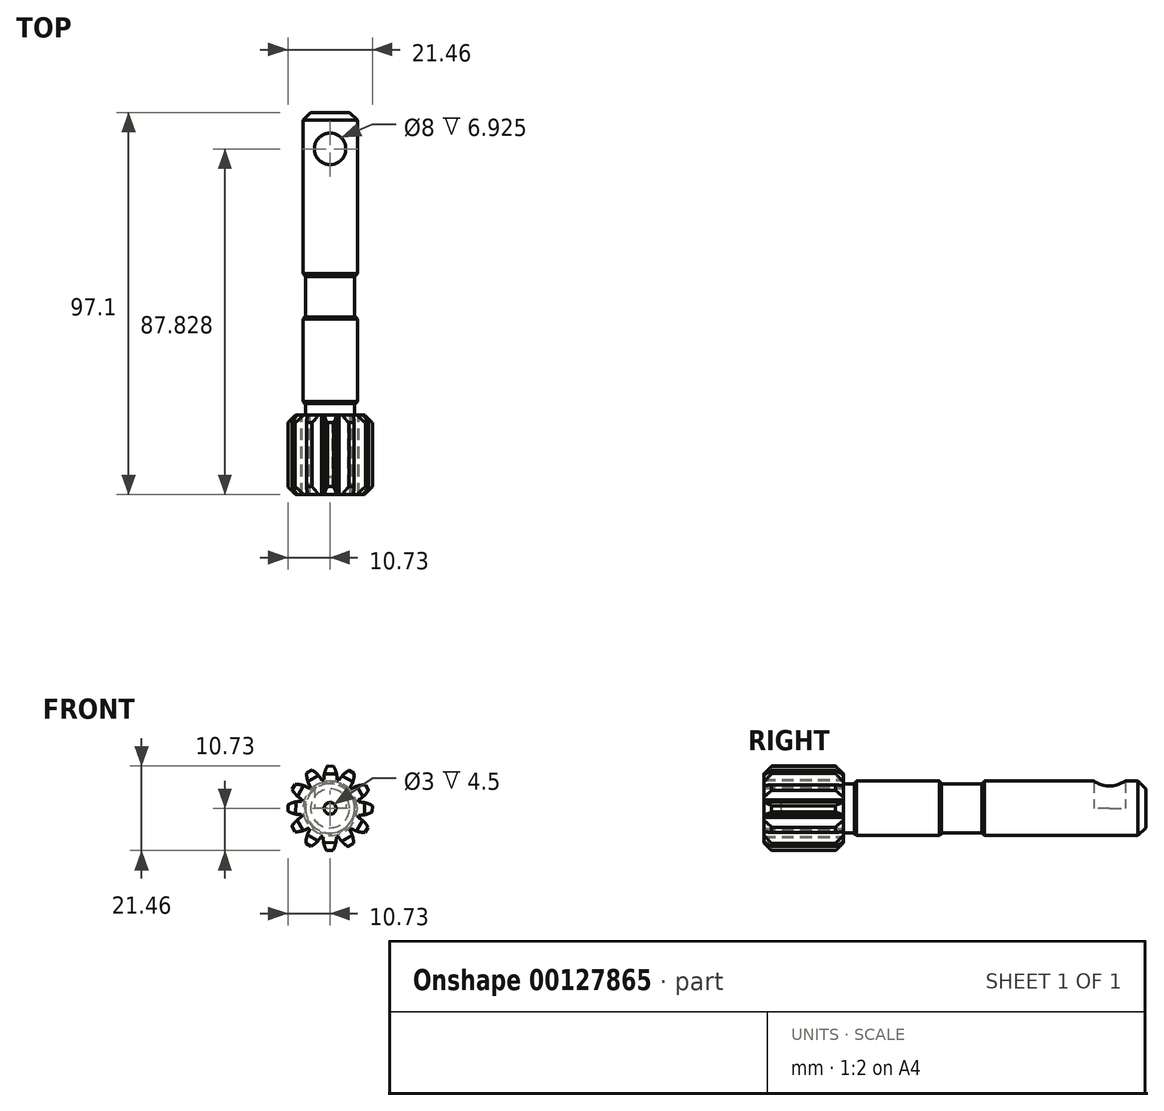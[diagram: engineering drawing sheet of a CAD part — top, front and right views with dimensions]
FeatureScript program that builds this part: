
annotation { "Feature Type Name" : "Feature", "Feature Type Description" : "" }
export const myFeature = defineFeature(function(context is Context, id is Id, definition is map)
    precondition{}
    {
        {
            var Q0;
            Q0=qCreatedBy(makeId("Front.planeOp"),FACE);
            var sketch = newSketch(context, id + "F0", { "sketchPlane" : qUnion([Q0])});
            skCircle(sketch, "E0", {"center": v(0, 0) * mm, "radius": 7.5 * mm});
            skCircle(sketch, "E1", {"center": v(0, 0) * mm, "radius": 10.75 * mm, "construction": true});
            skCircle(sketch, "E2", {"center": v(0, 0) * mm, "radius": 8.75 * mm, "construction": true});
            skArc(sketch, "E3", {"start": v(-0.67, 10.73) * mm, "mid": v(-1.38, 9.1) * mm, "end": v(-1.58, 7.33) * mm});
            skArc(sketch, "E4", {"start": v(1.73, 7.3) * mm, "mid": v(1.56, 9.07) * mm, "end": v(0.88, 10.71) * mm});
            skLineSegment(sketch, "E5", {"start": v(-0.67, 10.73) * mm, "end": v(0.88, 10.71) * mm});
            skLineSegment(sketch, "E6.1.0", {"start": v(-5.95, 8.95) * mm, "end": v(-4.6, 9.72) * mm});
            skArc(sketch, "E6.1.1", {"start": v(-2.15, 7.19) * mm, "mid": v(-3.18, 8.63) * mm, "end": v(-4.6, 9.72) * mm});
            skArc(sketch, "E6.1.2", {"start": v(-5.95, 8.95) * mm, "mid": v(-5.75, 7.19) * mm, "end": v(-5.04, 5.56) * mm});
            skLineSegment(sketch, "E6.2.0", {"start": v(-9.63, 4.78) * mm, "end": v(-8.84, 6.12) * mm});
            skArc(sketch, "E6.2.1", {"start": v(-5.45, 5.15) * mm, "mid": v(-7.07, 5.89) * mm, "end": v(-8.84, 6.12) * mm});
            skArc(sketch, "E6.2.2", {"start": v(-9.63, 4.78) * mm, "mid": v(-8.57, 3.35) * mm, "end": v(-7.14, 2.3) * mm});
            skLineSegment(sketch, "E6.3.0", {"start": v(-10.73, -0.67) * mm, "end": v(-10.71, 0.88) * mm});
            skArc(sketch, "E6.3.1", {"start": v(-7.3, 1.73) * mm, "mid": v(-9.07, 1.56) * mm, "end": v(-10.71, 0.88) * mm});
            skArc(sketch, "E6.3.2", {"start": v(-10.73, -0.67) * mm, "mid": v(-9.1, -1.38) * mm, "end": v(-7.33, -1.58) * mm});
            skLineSegment(sketch, "E6.4.0", {"start": v(-8.95, -5.95) * mm, "end": v(-9.72, -4.6) * mm});
            skArc(sketch, "E6.4.1", {"start": v(-7.19, -2.15) * mm, "mid": v(-8.63, -3.18) * mm, "end": v(-9.72, -4.6) * mm});
            skArc(sketch, "E6.4.2", {"start": v(-8.95, -5.95) * mm, "mid": v(-7.19, -5.75) * mm, "end": v(-5.56, -5.04) * mm});
            skLineSegment(sketch, "E6.5.0", {"start": v(-4.78, -9.63) * mm, "end": v(-6.12, -8.84) * mm});
            skArc(sketch, "E6.5.1", {"start": v(-5.15, -5.45) * mm, "mid": v(-5.89, -7.07) * mm, "end": v(-6.12, -8.84) * mm});
            skArc(sketch, "E6.5.2", {"start": v(-4.78, -9.63) * mm, "mid": v(-3.35, -8.57) * mm, "end": v(-2.3, -7.14) * mm});
            skLineSegment(sketch, "E6.6.0", {"start": v(0.67, -10.73) * mm, "end": v(-0.88, -10.71) * mm});
            skArc(sketch, "E6.6.1", {"start": v(-1.73, -7.3) * mm, "mid": v(-1.56, -9.07) * mm, "end": v(-0.88, -10.71) * mm});
            skArc(sketch, "E6.6.2", {"start": v(0.67, -10.73) * mm, "mid": v(1.38, -9.1) * mm, "end": v(1.58, -7.33) * mm});
            skLineSegment(sketch, "E6.7.0", {"start": v(5.95, -8.95) * mm, "end": v(4.6, -9.72) * mm});
            skArc(sketch, "E6.7.1", {"start": v(2.15, -7.19) * mm, "mid": v(3.18, -8.63) * mm, "end": v(4.6, -9.72) * mm});
            skArc(sketch, "E6.7.2", {"start": v(5.95, -8.95) * mm, "mid": v(5.75, -7.19) * mm, "end": v(5.04, -5.56) * mm});
            skLineSegment(sketch, "E6.8.0", {"start": v(9.63, -4.78) * mm, "end": v(8.84, -6.12) * mm});
            skArc(sketch, "E6.8.1", {"start": v(5.45, -5.15) * mm, "mid": v(7.07, -5.89) * mm, "end": v(8.84, -6.12) * mm});
            skArc(sketch, "E6.8.2", {"start": v(9.63, -4.78) * mm, "mid": v(8.57, -3.35) * mm, "end": v(7.14, -2.3) * mm});
            skLineSegment(sketch, "E6.9.0", {"start": v(10.73, 0.67) * mm, "end": v(10.71, -0.88) * mm});
            skArc(sketch, "E6.9.1", {"start": v(7.3, -1.73) * mm, "mid": v(9.07, -1.56) * mm, "end": v(10.71, -0.88) * mm});
            skArc(sketch, "E6.9.2", {"start": v(10.73, 0.67) * mm, "mid": v(9.1, 1.38) * mm, "end": v(7.33, 1.58) * mm});
            skLineSegment(sketch, "E6.10.0", {"start": v(8.95, 5.95) * mm, "end": v(9.72, 4.6) * mm});
            skArc(sketch, "E6.10.1", {"start": v(7.19, 2.15) * mm, "mid": v(8.63, 3.18) * mm, "end": v(9.72, 4.6) * mm});
            skArc(sketch, "E6.10.2", {"start": v(8.95, 5.95) * mm, "mid": v(7.19, 5.75) * mm, "end": v(5.56, 5.04) * mm});
            skLineSegment(sketch, "E6.11.0", {"start": v(4.78, 9.63) * mm, "end": v(6.12, 8.84) * mm});
            skArc(sketch, "E6.11.1", {"start": v(5.15, 5.45) * mm, "mid": v(5.89, 7.07) * mm, "end": v(6.12, 8.84) * mm});
            skArc(sketch, "E6.11.2", {"start": v(4.78, 9.63) * mm, "mid": v(3.35, 8.57) * mm, "end": v(2.3, 7.14) * mm});
            skSolve(sketch);
        }
        {
            var Q0;
            {var subQ0=sQuery(id+"F0.wireOp",EDGE,"E3");Q0=makeQuery(id+"F0.imprint","IMPRINT",FACE,{"disambiguationData":[TD([[makeQuery(id+"F0.imprint","IMPRINT",EDGE,{"derivedFrom":subQ0}),1.0]])]});}
            var Q1;
            {var subQ0=sQuery(id+"F0.wireOp",EDGE,"E0");var subQ15=makeQuery(id+"F0.imprint","INTERSECT",VERTEX,{"derivedFrom":[subQ0,sQuery(id+"F0.wireOp",EDGE,"E6.9.2")]});Q1=makeQuery(id+"F0.imprint","IMPRINT",FACE,{"disambiguationData":[TD([[makeQuery(id+"F0.imprint","IMPRINT",EDGE,{"disambiguationData":[TD([[subQ15,-1.0]])],"derivedFrom":subQ0}),1.0]])]});}
            var Q2;
            Q2=makeQuery(id+"F0.imprint","IMPRINT",FACE,{"disambiguationData":[TD([[makeQuery(id+"F0.imprint","IMPRINT",EDGE,{"derivedFrom":sQuery(id+"F0.wireOp",EDGE,"E6.4.0")}),-1.0]])]});
            var Q3;
            Q3=makeQuery(id+"F0.imprint","IMPRINT",FACE,{"disambiguationData":[TD([[makeQuery(id+"F0.imprint","IMPRINT",EDGE,{"derivedFrom":sQuery(id+"F0.wireOp",EDGE,"E6.3.0")}),-1.0]])]});
            var Q4;
            Q4=makeQuery(id+"F0.imprint","IMPRINT",FACE,{"disambiguationData":[TD([[makeQuery(id+"F0.imprint","IMPRINT",EDGE,{"derivedFrom":sQuery(id+"F0.wireOp",EDGE,"E6.2.0")}),-1.0]])]});
            var Q5;
            Q5=makeQuery(id+"F0.imprint","IMPRINT",FACE,{"disambiguationData":[TD([[makeQuery(id+"F0.imprint","IMPRINT",EDGE,{"derivedFrom":sQuery(id+"F0.wireOp",EDGE,"E6.1.0")}),-1.0]])]});
            var Q6;
            Q6=makeQuery(id+"F0.imprint","IMPRINT",FACE,{"disambiguationData":[TD([[makeQuery(id+"F0.imprint","IMPRINT",EDGE,{"derivedFrom":sQuery(id+"F0.wireOp",EDGE,"E6.5.0")}),-1.0]])]});
            var Q7;
            Q7=makeQuery(id+"F0.imprint","IMPRINT",FACE,{"disambiguationData":[TD([[makeQuery(id+"F0.imprint","IMPRINT",EDGE,{"derivedFrom":sQuery(id+"F0.wireOp",EDGE,"E6.6.0")}),-1.0]])]});
            var Q8;
            Q8=makeQuery(id+"F0.imprint","IMPRINT",FACE,{"disambiguationData":[TD([[makeQuery(id+"F0.imprint","IMPRINT",EDGE,{"derivedFrom":sQuery(id+"F0.wireOp",EDGE,"E6.7.0")}),-1.0]])]});
            var Q9;
            Q9=makeQuery(id+"F0.imprint","IMPRINT",FACE,{"disambiguationData":[TD([[makeQuery(id+"F0.imprint","IMPRINT",EDGE,{"derivedFrom":sQuery(id+"F0.wireOp",EDGE,"E6.8.0")}),-1.0]])]});
            var Q10;
            Q10=makeQuery(id+"F0.imprint","IMPRINT",FACE,{"disambiguationData":[TD([[makeQuery(id+"F0.imprint","IMPRINT",EDGE,{"derivedFrom":sQuery(id+"F0.wireOp",EDGE,"E6.9.0")}),-1.0]])]});
            var Q11;
            Q11=makeQuery(id+"F0.imprint","IMPRINT",FACE,{"disambiguationData":[TD([[makeQuery(id+"F0.imprint","IMPRINT",EDGE,{"derivedFrom":sQuery(id+"F0.wireOp",EDGE,"E6.10.0")}),-1.0]])]});
            var Q12;
            Q12=makeQuery(id+"F0.imprint","IMPRINT",FACE,{"disambiguationData":[TD([[makeQuery(id+"F0.imprint","IMPRINT",EDGE,{"derivedFrom":sQuery(id+"F0.wireOp",EDGE,"E6.11.0")}),-1.0]])]});
            extrude(context, id + "F1", {"entities" : qUnion([Q0, Q1, Q2, Q3, Q4, Q5, Q6, Q7, Q8, Q9, Q10, Q11, Q12]), "depth" : 20.25 * mm});
        }
        {
            var Q0;
            Q0=makeQuery(id+"F1.opExtrude","CAP_EDGE",EDGE,{"disambiguationData":[OSD([sQuery(id+"F0.wireOp",EDGE,"E6.11.0")])],"isStart":true});
            var Q1;
            Q1=makeQuery(id+"F1.opExtrude","CAP_EDGE",EDGE,{"disambiguationData":[OSD([sQuery(id+"F0.wireOp",EDGE,"E6.11.0")])],"isStart":false});
            var Q2;
            Q2=makeQuery(id+"F1.opExtrude","CAP_EDGE",EDGE,{"disambiguationData":[OSD([sQuery(id+"F0.wireOp",EDGE,"E5")])],"isStart":false});
            var Q3;
            Q3=makeQuery(id+"F1.opExtrude","CAP_EDGE",EDGE,{"disambiguationData":[OSD([sQuery(id+"F0.wireOp",EDGE,"E5")])],"isStart":true});
            var Q4;
            Q4=makeQuery(id+"F1.opExtrude","CAP_EDGE",EDGE,{"disambiguationData":[OSD([sQuery(id+"F0.wireOp",EDGE,"E6.1.0")])],"isStart":false});
            var Q5;
            Q5=makeQuery(id+"F1.opExtrude","CAP_EDGE",EDGE,{"disambiguationData":[OSD([sQuery(id+"F0.wireOp",EDGE,"E6.2.0")])],"isStart":false});
            var Q6;
            Q6=makeQuery(id+"F1.opExtrude","CAP_EDGE",EDGE,{"disambiguationData":[OSD([sQuery(id+"F0.wireOp",EDGE,"E6.3.0")])],"isStart":false});
            var Q7;
            Q7=makeQuery(id+"F1.opExtrude","CAP_EDGE",EDGE,{"disambiguationData":[OSD([sQuery(id+"F0.wireOp",EDGE,"E6.10.0")])],"isStart":false});
            var Q8;
            Q8=makeQuery(id+"F1.opExtrude","CAP_EDGE",EDGE,{"disambiguationData":[OSD([sQuery(id+"F0.wireOp",EDGE,"E6.9.0")])],"isStart":false});
            var Q9;
            Q9=makeQuery(id+"F1.opExtrude","CAP_EDGE",EDGE,{"disambiguationData":[OSD([sQuery(id+"F0.wireOp",EDGE,"E6.8.0")])],"isStart":false});
            var Q10;
            Q10=makeQuery(id+"F1.opExtrude","CAP_EDGE",EDGE,{"disambiguationData":[OSD([sQuery(id+"F0.wireOp",EDGE,"E6.7.0")])],"isStart":false});
            var Q11;
            Q11=makeQuery(id+"F1.opExtrude","CAP_EDGE",EDGE,{"disambiguationData":[OSD([sQuery(id+"F0.wireOp",EDGE,"E6.6.0")])],"isStart":false});
            var Q12;
            Q12=makeQuery(id+"F1.opExtrude","CAP_EDGE",EDGE,{"disambiguationData":[OSD([sQuery(id+"F0.wireOp",EDGE,"E6.5.0")])],"isStart":false});
            var Q13;
            Q13=makeQuery(id+"F1.opExtrude","CAP_EDGE",EDGE,{"disambiguationData":[OSD([sQuery(id+"F0.wireOp",EDGE,"E6.4.0")])],"isStart":false});
            var Q14;
            Q14=makeQuery(id+"F1.opExtrude","CAP_EDGE",EDGE,{"disambiguationData":[OSD([sQuery(id+"F0.wireOp",EDGE,"E6.10.0")])],"isStart":true});
            var Q15;
            Q15=makeQuery(id+"F1.opExtrude","CAP_EDGE",EDGE,{"disambiguationData":[OSD([sQuery(id+"F0.wireOp",EDGE,"E6.9.0")])],"isStart":true});
            var Q16;
            Q16=makeQuery(id+"F1.opExtrude","CAP_EDGE",EDGE,{"disambiguationData":[OSD([sQuery(id+"F0.wireOp",EDGE,"E6.8.0")])],"isStart":true});
            var Q17;
            Q17=makeQuery(id+"F1.opExtrude","CAP_EDGE",EDGE,{"disambiguationData":[OSD([sQuery(id+"F0.wireOp",EDGE,"E6.7.0")])],"isStart":true});
            var Q18;
            Q18=makeQuery(id+"F1.opExtrude","CAP_EDGE",EDGE,{"disambiguationData":[OSD([sQuery(id+"F0.wireOp",EDGE,"E6.6.0")])],"isStart":true});
            var Q19;
            Q19=makeQuery(id+"F1.opExtrude","CAP_EDGE",EDGE,{"disambiguationData":[OSD([sQuery(id+"F0.wireOp",EDGE,"E6.5.0")])],"isStart":true});
            var Q20;
            Q20=makeQuery(id+"F1.opExtrude","CAP_EDGE",EDGE,{"disambiguationData":[OSD([sQuery(id+"F0.wireOp",EDGE,"E6.4.0")])],"isStart":true});
            var Q21;
            Q21=makeQuery(id+"F1.opExtrude","CAP_EDGE",EDGE,{"disambiguationData":[OSD([sQuery(id+"F0.wireOp",EDGE,"E6.1.0")])],"isStart":true});
            var Q22;
            Q22=makeQuery(id+"F1.opExtrude","CAP_EDGE",EDGE,{"disambiguationData":[OSD([sQuery(id+"F0.wireOp",EDGE,"E6.2.0")])],"isStart":true});
            var Q23;
            Q23=makeQuery(id+"F1.opExtrude","CAP_EDGE",EDGE,{"disambiguationData":[OSD([sQuery(id+"F0.wireOp",EDGE,"E6.3.0")])],"isStart":true});
            chamfer(context, id + "F2", {"entities" : qUnion([Q0, Q1, Q2, Q3, Q4, Q5, Q6, Q7, Q8, Q9, Q10, Q11, Q12, Q13, Q14, Q15, Q16, Q17, Q18, Q19, Q20, Q21, Q22, Q23]), "chamferType" : ChamferType.OFFSET_ANGLE, "width" : 2 * mm, "oppositeDirection" : false, "angle" : 45 * degree, "tangentPropagation" : true});
        }
        {
            var Q0;
            Q0=makeQuery(id+"F1.opExtrude","CAP_FACE",FACE,{"disambiguationData":[OSD([sQuery(id+"F0.wireOp",EDGE,"E0"),sQuery(id+"F0.wireOp",EDGE,"E3"),sQuery(id+"F0.wireOp",EDGE,"E4"),sQuery(id+"F0.wireOp",EDGE,"E5"),sQuery(id+"F0.wireOp",EDGE,"E6.1.0"),sQuery(id+"F0.wireOp",EDGE,"E6.1.1"),sQuery(id+"F0.wireOp",EDGE,"E6.1.2"),sQuery(id+"F0.wireOp",EDGE,"E6.2.0"),sQuery(id+"F0.wireOp",EDGE,"E6.2.1"),sQuery(id+"F0.wireOp",EDGE,"E6.2.2"),sQuery(id+"F0.wireOp",EDGE,"E6.3.0"),sQuery(id+"F0.wireOp",EDGE,"E6.3.1"),sQuery(id+"F0.wireOp",EDGE,"E6.3.2"),sQuery(id+"F0.wireOp",EDGE,"E6.4.0"),sQuery(id+"F0.wireOp",EDGE,"E6.4.1"),sQuery(id+"F0.wireOp",EDGE,"E6.4.2"),sQuery(id+"F0.wireOp",EDGE,"E6.5.0"),sQuery(id+"F0.wireOp",EDGE,"E6.5.1"),sQuery(id+"F0.wireOp",EDGE,"E6.5.2"),sQuery(id+"F0.wireOp",EDGE,"E6.6.0"),sQuery(id+"F0.wireOp",EDGE,"E6.6.1"),sQuery(id+"F0.wireOp",EDGE,"E6.6.2"),sQuery(id+"F0.wireOp",EDGE,"E6.7.0"),sQuery(id+"F0.wireOp",EDGE,"E6.7.1"),sQuery(id+"F0.wireOp",EDGE,"E6.7.2"),sQuery(id+"F0.wireOp",EDGE,"E6.8.0"),sQuery(id+"F0.wireOp",EDGE,"E6.8.1"),sQuery(id+"F0.wireOp",EDGE,"E6.8.2"),sQuery(id+"F0.wireOp",EDGE,"E6.9.0"),sQuery(id+"F0.wireOp",EDGE,"E6.9.1"),sQuery(id+"F0.wireOp",EDGE,"E6.9.2"),sQuery(id+"F0.wireOp",EDGE,"E6.10.0"),sQuery(id+"F0.wireOp",EDGE,"E6.10.1"),sQuery(id+"F0.wireOp",EDGE,"E6.10.2"),sQuery(id+"F0.wireOp",EDGE,"E6.11.0"),sQuery(id+"F0.wireOp",EDGE,"E6.11.1"),sQuery(id+"F0.wireOp",EDGE,"E6.11.2")])],"isStart":false});
            var sketch = newSketch(context, id + "F3", { "sketchPlane" : qUnion([Q0])});
            skPoint(sketch, "E7", {"position": v(0, 0) * mm});
            skCircle(sketch, "E8", {"center": v(0, 0) * mm, "radius": 1.5 * mm});
            skSolve(sketch);
        }
        {
            var Q0;
            Q0=makeQuery(id+"F3.imprint","IMPRINT",FACE,{"disambiguationData":[TD([[makeQuery(id+"F3.imprint","IMPRINT",EDGE,{"derivedFrom":sQuery(id+"F3.wireOp",EDGE,"E8")}),1.0]])]});
            extrude(context, id + "F4", {"entities" : qUnion([Q0]), "operationType" : NewBodyOperationType.REMOVE, "oppositeDirection" : true, "depth" : 4.5 * mm});
        }
        {
            var Q0;
            Q0=makeQuery(id+"F1.opExtrude","CAP_FACE",FACE,{"disambiguationData":[OSD([sQuery(id+"F0.wireOp",EDGE,"E0"),sQuery(id+"F0.wireOp",EDGE,"E3"),sQuery(id+"F0.wireOp",EDGE,"E4"),sQuery(id+"F0.wireOp",EDGE,"E5"),sQuery(id+"F0.wireOp",EDGE,"E6.1.0"),sQuery(id+"F0.wireOp",EDGE,"E6.1.1"),sQuery(id+"F0.wireOp",EDGE,"E6.1.2"),sQuery(id+"F0.wireOp",EDGE,"E6.2.0"),sQuery(id+"F0.wireOp",EDGE,"E6.2.1"),sQuery(id+"F0.wireOp",EDGE,"E6.2.2"),sQuery(id+"F0.wireOp",EDGE,"E6.3.0"),sQuery(id+"F0.wireOp",EDGE,"E6.3.1"),sQuery(id+"F0.wireOp",EDGE,"E6.3.2"),sQuery(id+"F0.wireOp",EDGE,"E6.4.0"),sQuery(id+"F0.wireOp",EDGE,"E6.4.1"),sQuery(id+"F0.wireOp",EDGE,"E6.4.2"),sQuery(id+"F0.wireOp",EDGE,"E6.5.0"),sQuery(id+"F0.wireOp",EDGE,"E6.5.1"),sQuery(id+"F0.wireOp",EDGE,"E6.5.2"),sQuery(id+"F0.wireOp",EDGE,"E6.6.0"),sQuery(id+"F0.wireOp",EDGE,"E6.6.1"),sQuery(id+"F0.wireOp",EDGE,"E6.6.2"),sQuery(id+"F0.wireOp",EDGE,"E6.7.0"),sQuery(id+"F0.wireOp",EDGE,"E6.7.1"),sQuery(id+"F0.wireOp",EDGE,"E6.7.2"),sQuery(id+"F0.wireOp",EDGE,"E6.8.0"),sQuery(id+"F0.wireOp",EDGE,"E6.8.1"),sQuery(id+"F0.wireOp",EDGE,"E6.8.2"),sQuery(id+"F0.wireOp",EDGE,"E6.9.0"),sQuery(id+"F0.wireOp",EDGE,"E6.9.1"),sQuery(id+"F0.wireOp",EDGE,"E6.9.2"),sQuery(id+"F0.wireOp",EDGE,"E6.10.0"),sQuery(id+"F0.wireOp",EDGE,"E6.10.1"),sQuery(id+"F0.wireOp",EDGE,"E6.10.2"),sQuery(id+"F0.wireOp",EDGE,"E6.11.0"),sQuery(id+"F0.wireOp",EDGE,"E6.11.1"),sQuery(id+"F0.wireOp",EDGE,"E6.11.2")])],"isStart":true});
            var sketch = newSketch(context, id + "F5", { "sketchPlane" : qUnion([Q0])});
            skCircle(sketch, "E9", {"center": v(0, 0) * mm, "radius": 6.22 * mm});
            skSolve(sketch);
        }
        {
            var Q0;
            Q0 = qSketchRegion(id + "F5", true);
            extrude(context, id + "F6", {"entities" : qUnion([Q0]), "operationType" : NewBodyOperationType.ADD, "depth" : 2.85 * mm});
        }
        {
            var Q0;
            Q0=makeQuery(id+"F6.opExtrude","CAP_FACE",FACE,{"disambiguationData":[OSD([sQuery(id+"F5.wireOp",EDGE,"E9")])],"isStart":false});
            var sketch = newSketch(context, id + "F7", { "sketchPlane" : qUnion([Q0])});
            skCircle(sketch, "E10", {"center": v(0, 0) * mm, "radius": 6.93 * mm});
            skSolve(sketch);
        }
        {
            var Q0;
            Q0 = qSketchRegion(id + "F7", true);
            extrude(context, id + "F8", {"entities" : qUnion([Q0]), "operationType" : NewBodyOperationType.ADD, "depth" : 22 * mm});
        }
        {
            var Q0;
            Q0=makeQuery(id+"F8.opExtrude","CAP_FACE",FACE,{"disambiguationData":[OSD([sQuery(id+"F7.wireOp",EDGE,"E10")])],"isStart":false});
            var sketch = newSketch(context, id + "F9", { "sketchPlane" : qUnion([Q0])});
            skCircle(sketch, "E11", {"center": v(0, 0) * mm, "radius": 6.23 * mm});
            skSolve(sketch);
        }
        {
            var Q0;
            Q0 = qSketchRegion(id + "F9", true);
            extrude(context, id + "F10", {"entities" : qUnion([Q0]), "operationType" : NewBodyOperationType.ADD, "depth" : 9 * mm});
        }
        {
            var Q0;
            Q0=makeQuery(id+"F8.opExtrude","SWEPT_FACE",FACE,{"disambiguationData":[OSD([sQuery(id+"F7.wireOp",EDGE,"E10")])]});
            chamfer(context, id + "F11", {"entities" : qUnion([Q0]), "chamferType" : ChamferType.OFFSET_ANGLE, "width" : .5 * mm, "oppositeDirection" : false, "angle" : 45 * degree, "tangentPropagation" : true});
        }
        {
            var Q0;
            Q0=makeQuery(id+"F10.opExtrude","CAP_FACE",FACE,{"disambiguationData":[OSD([sQuery(id+"F9.wireOp",EDGE,"E11")])],"isStart":false});
            var sketch = newSketch(context, id + "F12", { "sketchPlane" : qUnion([Q0])});
            skCircle(sketch, "E12", {"center": v(0, 0) * mm, "radius": 6.92 * mm});
            skSolve(sketch);
        }
        {
            var Q0;
            Q0 = qSketchRegion(id + "F12", true);
            extrude(context, id + "F13", {"entities" : qUnion([Q0]), "operationType" : NewBodyOperationType.ADD, "depth" : 43 * mm});
        }
        {
            var Q0;
            Q0=makeQuery(id+"F13.opExtrude","SWEPT_FACE",FACE,{"disambiguationData":[OSD([sQuery(id+"F12.wireOp",EDGE,"E12")])]});
            chamfer(context, id + "F14", {"entities" : qUnion([Q0]), "chamferType" : ChamferType.OFFSET_ANGLE, "width" : 2 * mm, "oppositeDirection" : false, "angle" : 45 * degree, "tangentPropagation" : true});
        }
        {
            var Q0;
            Q0=qCreatedBy(makeId("Top.planeOp"),FACE);
            var sketch = newSketch(context, id + "F15", { "sketchPlane" : qUnion([Q0])});
            skLineSegment(sketch, "E13", {"start": v(-6.92, 35.85) * mm, "end": v(-6.92, 74.85) * mm});
            skLineSegment(sketch, "E14", {"start": v(6.92, 74.85) * mm, "end": v(6.92, 35.85) * mm});
            skCircle(sketch, "E15", {"center": v(0, 67.58) * mm, "radius": 4 * mm});
            skSolve(sketch);
        }
        {
            var Q0;
            Q0 = qSketchRegion(id + "F15", true);
            extrude(context, id + "F16", {"entities" : qUnion([Q0]), "operationType" : NewBodyOperationType.REMOVE, "depth" : 9.5 * mm});
        }
    });
